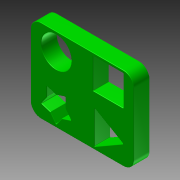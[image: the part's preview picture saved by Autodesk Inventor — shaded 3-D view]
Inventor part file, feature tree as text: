
AUTODESK INVENTOR PART (.ipt)
format: ipt  version: 2015 (Build 190159000, 159)  size: 256,512 bytes
history: native  units: in
note: dims shown in document units (in); Inventor stores cm internally (conversion verified against a paired STEP export)
features: extrude x1, fillet x1, shell x1, sketch x1
ambient origin geometry x8: Origin, YZ Plane, XZ Plane, XY Plane, X Axis, Y Axis, Z Axis, Center Point
bodies: Solid1 (feature_tree)
feature tree (4):
  extrude  "Extrusion1"  Depth=1.59in
  fillet  "Fillet1"  Radius=0.2in
  shell  "Shell1"  Thickness=0.6051in
  sketch  "Sketch1"  dims[d0=1.975in d1=1.59in d2=0.2in d3=0.6051in d4=0.187in d5=0.58in d6=0.638in d7=0.58in d8=0.05in d9=0.05in d10=0.05in d11=0.05in d12=0.2in d13=0.2in d14=0.2in d15=0.2in d16=0.3in d17=0.0in d18=0.01in d19=0.01in]
